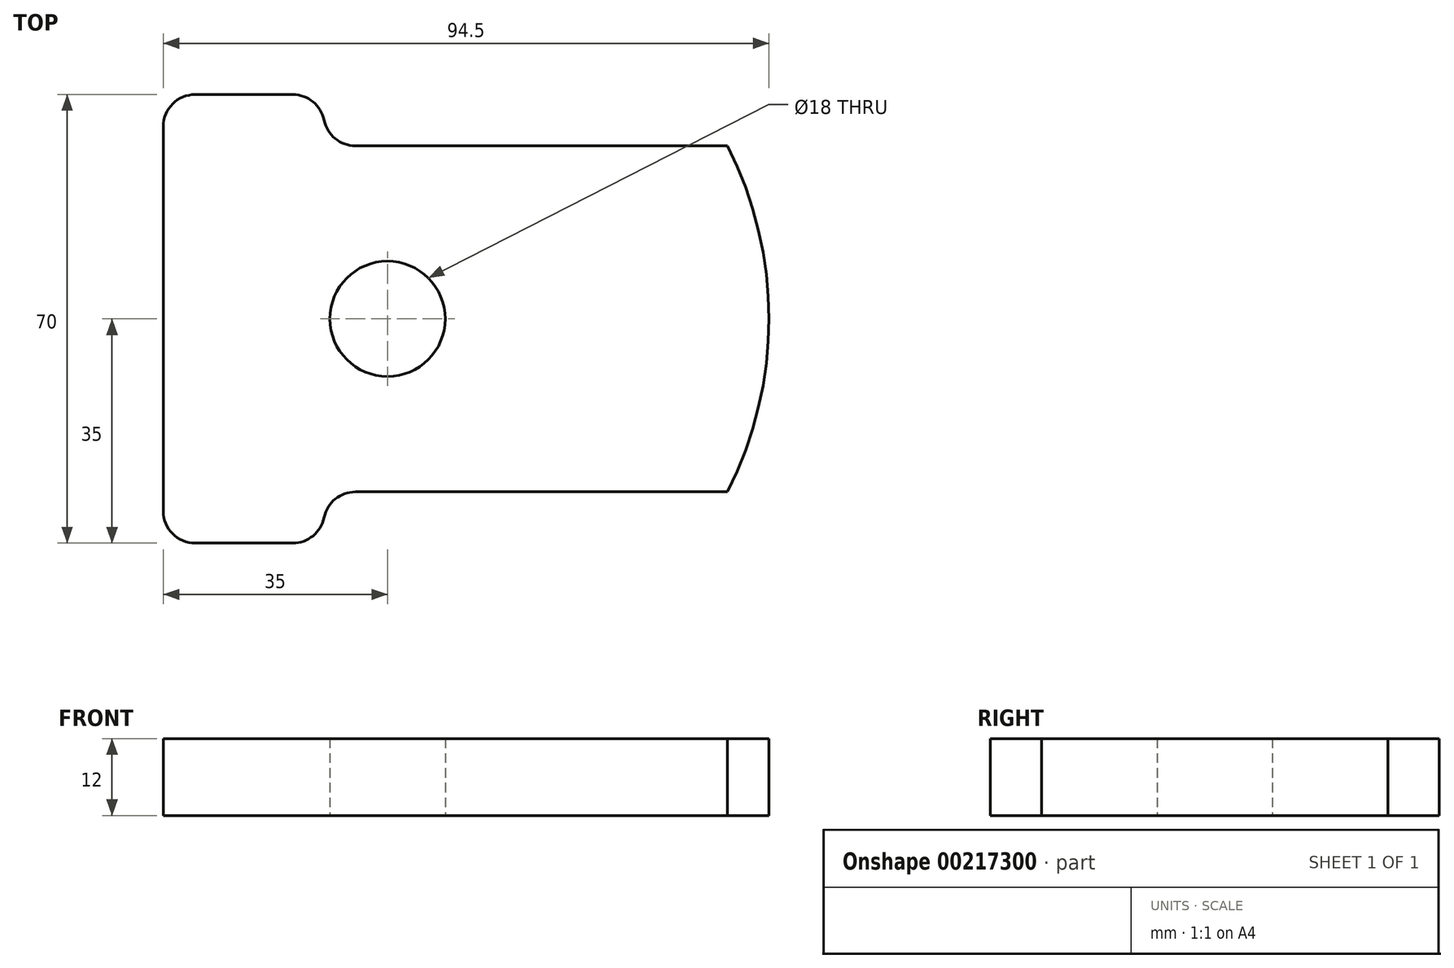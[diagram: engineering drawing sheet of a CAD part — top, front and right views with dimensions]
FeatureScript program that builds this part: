
annotation { "Feature Type Name" : "Feature", "Feature Type Description" : "" }
export const myFeature = defineFeature(function(context is Context, id is Id, definition is map)
    precondition{}
    {
        {
            var Q0;
            Q0=qCreatedBy(makeId("Top.planeOp"),FACE);
            var sketch = newSketch(context, id + "F0", { "sketchPlane" : qUnion([Q0])});
            skCircle(sketch, "E0", {"center": v(0, 0) * mm, "radius": 9 * mm});
            skLineSegment(sketch, "E1.bottom", {"start": v(-35, 35) * mm, "end": v(-10, 35) * mm});
            skLineSegment(sketch, "E1.top", {"start": v(-35, -35) * mm, "end": v(-10, -35) * mm});
            skLineSegment(sketch, "E1.left", {"start": v(-35, 35) * mm, "end": v(-35, -35) * mm});
            skLineSegment(sketch, "E2", {"start": v(-10, 35) * mm, "end": v(-10, 27) * mm});
            skLineSegment(sketch, "E3", {"start": v(-10, -27) * mm, "end": v(-10, -35) * mm});
            skLineSegment(sketch, "E4", {"start": v(-10, 27) * mm, "end": v(53.02, 27) * mm});
            skLineSegment(sketch, "E5", {"start": v(-10, -27) * mm, "end": v(53.02, -27) * mm});
            skArc(sketch, "E6", {"start": v(53.02, -27) * mm, "mid": v(59.5, 0) * mm, "end": v(53.02, 27) * mm});
            skSolve(sketch);
        }
        {
            var Q0;
            Q0=makeQuery(id+"F0.imprint","IMPRINT",FACE,{"disambiguationData":[TD([[makeQuery(id+"F0.imprint","IMPRINT",EDGE,{"derivedFrom":sQuery(id+"F0.wireOp",EDGE,"E0")}),-1.0]])]});
            extrude(context, id + "F1", {"entities" : qUnion([Q0]), "depth" : 12 * mm});
        }
        {
            var Q0;
            Q0=makeQuery(id+"F1.opExtrude","SWEPT_EDGE",EDGE,{"disambiguationData":[OSD([sQuery(id+"F0.wireOp",EDGE,"E3"),sQuery(id+"F0.wireOp",EDGE,"E5")])]});
            fillet(context, id + "F2", {"entities" : qUnion([Q0]), "radius" : 5 * mm, "tangentPropagation" : true, "allowEdgeOverflow" : false});
        }
        {
            var Q0;
            Q0=makeQuery(id+"F1.opExtrude","SWEPT_EDGE",EDGE,{"disambiguationData":[OSD([sQuery(id+"F0.wireOp",EDGE,"E2"),sQuery(id+"F0.wireOp",EDGE,"E4")])]});
            fillet(context, id + "F3", {"entities" : qUnion([Q0]), "radius" : 5 * mm, "tangentPropagation" : true, "allowEdgeOverflow" : false});
        }
        {
            var Q0;
            Q0=makeQuery(id+"F1.opExtrude","SWEPT_EDGE",EDGE,{"disambiguationData":[OSD([sQuery(id+"F0.wireOp",EDGE,"E1.top"),sQuery(id+"F0.wireOp",EDGE,"E3")])]});
            fillet(context, id + "F4", {"entities" : qUnion([Q0]), "radius" : 5 * mm, "tangentPropagation" : true, "allowEdgeOverflow" : false});
        }
        {
            var Q0;
            Q0=makeQuery(id+"F1.opExtrude","SWEPT_EDGE",EDGE,{"disambiguationData":[OSD([sQuery(id+"F0.wireOp",EDGE,"E1.bottom"),sQuery(id+"F0.wireOp",EDGE,"E2")])]});
            fillet(context, id + "F5", {"entities" : qUnion([Q0]), "radius" : 5 * mm, "tangentPropagation" : true, "allowEdgeOverflow" : false});
        }
        {
            var Q0;
            Q0=makeQuery(id+"F1.opExtrude","SWEPT_EDGE",EDGE,{"disambiguationData":[OSD([sQuery(id+"F0.wireOp",EDGE,"E1.top"),sQuery(id+"F0.wireOp",EDGE,"E1.left")])]});
            var Q1;
            Q1=makeQuery(id+"F1.opExtrude","SWEPT_EDGE",EDGE,{"disambiguationData":[OSD([sQuery(id+"F0.wireOp",EDGE,"E1.bottom"),sQuery(id+"F0.wireOp",EDGE,"E1.left")])]});
            fillet(context, id + "F6", {"entities" : qUnion([Q0, Q1]), "radius" : 5 * mm, "tangentPropagation" : true, "allowEdgeOverflow" : false});
        }
    });
